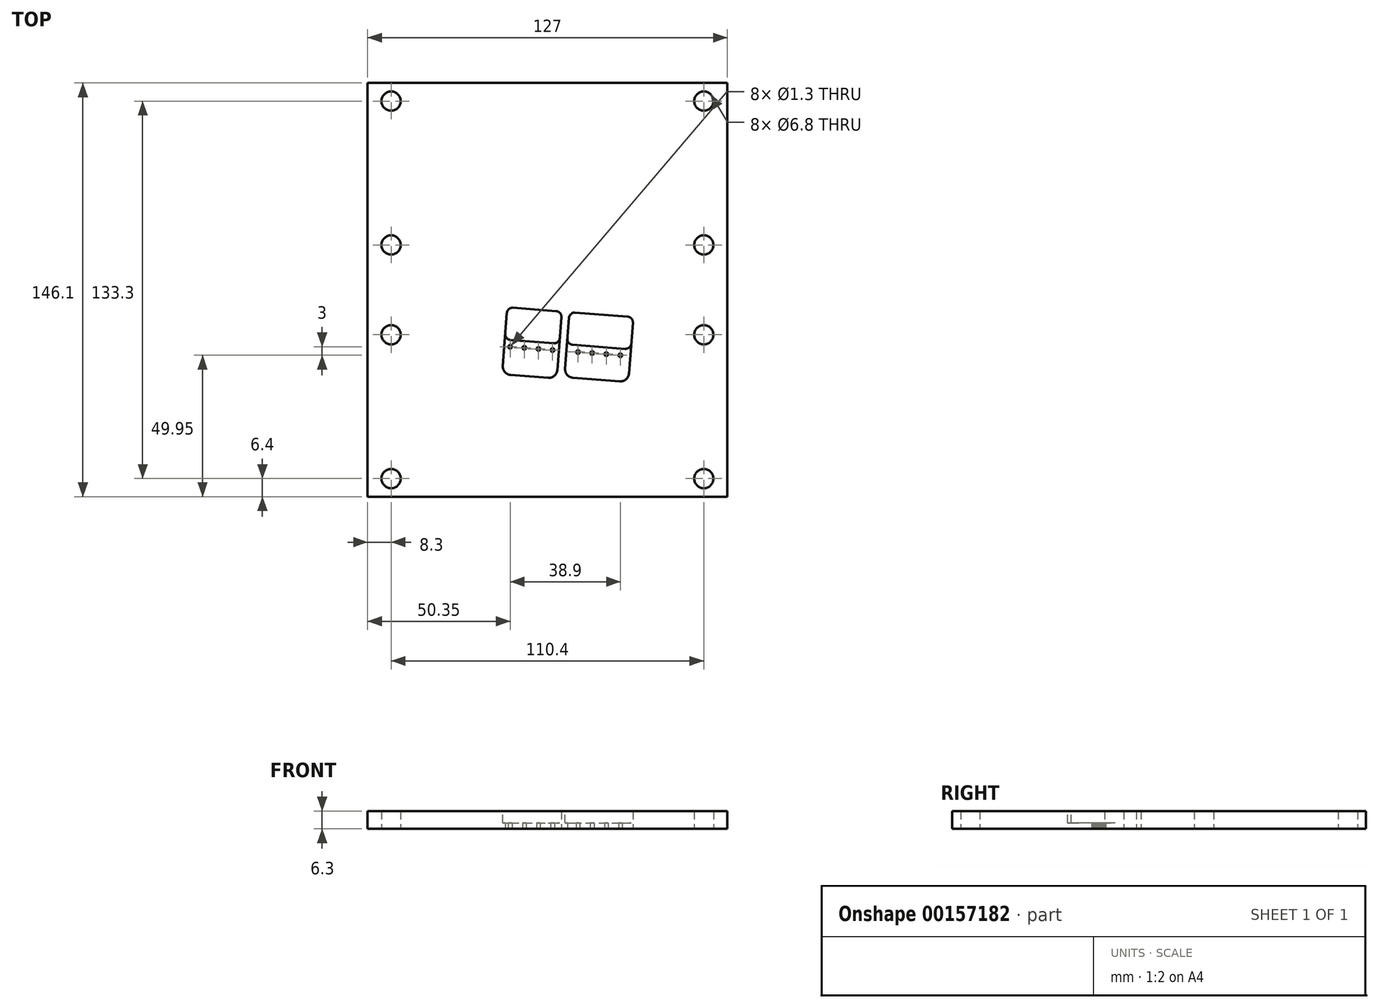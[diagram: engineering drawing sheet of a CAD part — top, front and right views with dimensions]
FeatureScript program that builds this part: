
annotation { "Feature Type Name" : "Feature", "Feature Type Description" : "" }
export const myFeature = defineFeature(function(context is Context, id is Id, definition is map)
    precondition{}
    {
        {
            var Q0;
            Q0=qCreatedBy(makeId("Top.planeOp"),FACE);
            var sketch = newSketch(context, id + "F0", { "sketchPlane" : qUnion([Q0])});
            skLineSegment(sketch, "E0.bottom", {"start": v(-63.5, 73.05) * mm, "end": v(63.5, 73.05) * mm});
            skLineSegment(sketch, "E0.top", {"start": v(-63.5, -73.05) * mm, "end": v(63.5, -73.05) * mm});
            skLineSegment(sketch, "E0.left", {"start": v(-63.5, 73.05) * mm, "end": v(-63.5, -73.05) * mm});
            skLineSegment(sketch, "E0.right", {"start": v(63.5, 73.05) * mm, "end": v(63.5, -73.05) * mm});
            skPoint(sketch, "E0.middle", {"position": v(0, 0) * mm});
            skLineSegment(sketch, "E1", {"start": v(-55.2, 73.05) * mm, "end": v(-55.2, -73.05) * mm, "construction": true});
            skLineSegment(sketch, "E2", {"start": v(55.2, 73.05) * mm, "end": v(55.2, -73.05) * mm, "construction": true});
            skCircle(sketch, "E3", {"center": v(-55.2, 66.65) * mm, "radius": 3.4 * mm});
            skCircle(sketch, "E4", {"center": v(-55.2, 15.85) * mm, "radius": 3.4 * mm});
            skCircle(sketch, "E5", {"center": v(-55.2, -15.85) * mm, "radius": 3.4 * mm});
            skCircle(sketch, "E6", {"center": v(-55.2, -66.65) * mm, "radius": 3.4 * mm});
            skCircle(sketch, "E7", {"center": v(55.2, -66.65) * mm, "radius": 3.4 * mm});
            skCircle(sketch, "E8", {"center": v(55.2, -15.85) * mm, "radius": 3.4 * mm});
            skCircle(sketch, "E9", {"center": v(55.2, 15.85) * mm, "radius": 3.4 * mm});
            skCircle(sketch, "E10", {"center": v(55.2, 66.65) * mm, "radius": 3.4 * mm});
            skCircle(sketch, "E11", {"center": v(25.75, -23.1) * mm, "radius": 0.65 * mm});
            skCircle(sketch, "E12", {"center": v(20.76, -22.72) * mm, "radius": 0.65 * mm});
            skCircle(sketch, "E13", {"center": v(15.78, -22.33) * mm, "radius": 0.65 * mm});
            skCircle(sketch, "E14", {"center": v(10.8, -21.95) * mm, "radius": 0.65 * mm});
            skCircle(sketch, "E15", {"center": v(1.8, -21.25) * mm, "radius": 0.65 * mm});
            skCircle(sketch, "E16", {"center": v(-3.18, -20.87) * mm, "radius": 0.65 * mm});
            skCircle(sketch, "E17", {"center": v(-8.16, -20.48) * mm, "radius": 0.65 * mm});
            skCircle(sketch, "E18", {"center": v(-13.15, -20.1) * mm, "radius": 0.65 * mm});
            skLineSegment(sketch, "E19", {"start": v(-13.15, -20.1) * mm, "end": v(25.75, -23.1) * mm, "construction": true});
            skLineSegment(sketch, "E20", {"start": v(-13.05, -17.7) * mm, "end": v(2.2, -18.88) * mm});
            skLineSegment(sketch, "E21", {"start": v(-12.17, -6.33) * mm, "end": v(3.08, -7.51) * mm});
            skLineSegment(sketch, "E22", {"start": v(-14.32, -8.17) * mm, "end": v(-14.89, -15.55) * mm});
            skLineSegment(sketch, "E23", {"start": v(4.92, -9.66) * mm, "end": v(4.35, -17.04) * mm});
            skLineSegment(sketch, "E24", {"start": v(7.61, -9.87) * mm, "end": v(7.04, -17.24) * mm});
            skLineSegment(sketch, "E25", {"start": v(30.15, -11.6) * mm, "end": v(29.58, -18.98) * mm});
            skLineSegment(sketch, "E26.trimOffspring", {"start": v(9.76, -8.03) * mm, "end": v(28.3, -9.46) * mm});
            skLineSegment(sketch, "E27.trimOffspring", {"start": v(8.89, -19.4) * mm, "end": v(27.43, -20.82) * mm});
            skPoint(sketch, "E28.visualSharp", {"position": v(-14.17, -6.18) * mm});
            skArc(sketch, "E28.filletArc", {"start": v(-12.17, -6.33) * mm, "mid": v(-13.63, -6.8) * mm, "end": v(-14.32, -8.17) * mm});
            skPoint(sketch, "E29.visualSharp", {"position": v(5.08, -7.66) * mm});
            skArc(sketch, "E29.filletArc", {"start": v(4.92, -9.66) * mm, "mid": v(4.45, -8.2) * mm, "end": v(3.08, -7.51) * mm});
            skPoint(sketch, "E30.visualSharp", {"position": v(-15.04, -17.55) * mm});
            skArc(sketch, "E30.filletArc", {"start": v(-14.89, -15.55) * mm, "mid": v(-14.41, -17) * mm, "end": v(-13.05, -17.7) * mm});
            skPoint(sketch, "E31.visualSharp", {"position": v(4.2, -19.03) * mm});
            skArc(sketch, "E31.filletArc", {"start": v(2.2, -18.88) * mm, "mid": v(3.66, -18.4) * mm, "end": v(4.35, -17.04) * mm});
            skPoint(sketch, "E32.visualSharp", {"position": v(7.77, -7.87) * mm});
            skArc(sketch, "E32.filletArc", {"start": v(9.76, -8.03) * mm, "mid": v(8.3, -8.5) * mm, "end": v(7.61, -9.87) * mm});
            skPoint(sketch, "E33.visualSharp", {"position": v(6.9, -19.24) * mm});
            skArc(sketch, "E33.filletArc", {"start": v(7.04, -17.24) * mm, "mid": v(7.52, -18.7) * mm, "end": v(8.89, -19.4) * mm});
            skPoint(sketch, "E34.visualSharp", {"position": v(30.3, -9.6) * mm});
            skArc(sketch, "E34.filletArc", {"start": v(30.15, -11.6) * mm, "mid": v(29.67, -10.15) * mm, "end": v(28.3, -9.46) * mm});
            skPoint(sketch, "E35.visualSharp", {"position": v(29.42, -20.98) * mm});
            skArc(sketch, "E35.filletArc", {"start": v(27.43, -20.82) * mm, "mid": v(28.89, -20.35) * mm, "end": v(29.58, -18.98) * mm});
            skSolve(sketch);
        }
        {
            var Q0;
            Q0 = qSketchRegion(id + "F0", true);
            extrude(context, id + "F1", {"entities" : qUnion([Q0]), "depth" : 6.3 * mm});
        }
        {
            var Q0;
            Q0=makeQuery(id+"F1.opExtrude","CAP_FACE",FACE,{"disambiguationData":[OSD([sQuery(id+"F0.wireOp",EDGE,"E0.bottom"),sQuery(id+"F0.wireOp",EDGE,"E0.top"),sQuery(id+"F0.wireOp",EDGE,"E0.left"),sQuery(id+"F0.wireOp",EDGE,"E0.right"),sQuery(id+"F0.wireOp",EDGE,"E3"),sQuery(id+"F0.wireOp",EDGE,"E4"),sQuery(id+"F0.wireOp",EDGE,"E5"),sQuery(id+"F0.wireOp",EDGE,"E6"),sQuery(id+"F0.wireOp",EDGE,"E7"),sQuery(id+"F0.wireOp",EDGE,"E8"),sQuery(id+"F0.wireOp",EDGE,"E9"),sQuery(id+"F0.wireOp",EDGE,"E10"),sQuery(id+"F0.wireOp",EDGE,"E11"),sQuery(id+"F0.wireOp",EDGE,"E12"),sQuery(id+"F0.wireOp",EDGE,"E13"),sQuery(id+"F0.wireOp",EDGE,"E14"),sQuery(id+"F0.wireOp",EDGE,"E15"),sQuery(id+"F0.wireOp",EDGE,"E16"),sQuery(id+"F0.wireOp",EDGE,"E17"),sQuery(id+"F0.wireOp",EDGE,"E18"),sQuery(id+"F0.wireOp",EDGE,"E20"),sQuery(id+"F0.wireOp",EDGE,"E21"),sQuery(id+"F0.wireOp",EDGE,"E22"),sQuery(id+"F0.wireOp",EDGE,"E23"),sQuery(id+"F0.wireOp",EDGE,"E24"),sQuery(id+"F0.wireOp",EDGE,"E25"),sQuery(id+"F0.wireOp",EDGE,"E26.trimOffspring"),sQuery(id+"F0.wireOp",EDGE,"E27.trimOffspring"),sQuery(id+"F0.wireOp",EDGE,"E28.filletArc"),sQuery(id+"F0.wireOp",EDGE,"E29.filletArc"),sQuery(id+"F0.wireOp",EDGE,"E30.filletArc"),sQuery(id+"F0.wireOp",EDGE,"E31.filletArc"),sQuery(id+"F0.wireOp",EDGE,"E32.filletArc"),sQuery(id+"F0.wireOp",EDGE,"E33.filletArc"),sQuery(id+"F0.wireOp",EDGE,"E34.filletArc"),sQuery(id+"F0.wireOp",EDGE,"E35.filletArc")])],"isStart":false});
            var sketch = newSketch(context, id + "F2", { "sketchPlane" : qUnion([Q0])});
            skLineSegment(sketch, "E36", {"start": v(-14.78, -14.1) * mm, "end": v(-15.76, -26.82) * mm});
            skLineSegment(sketch, "E37", {"start": v(-13, -30.04) * mm, "end": v(0.26, -31.06) * mm});
            skLineSegment(sketch, "E38", {"start": v(4.46, -15.58) * mm, "end": v(3.48, -28.3) * mm});
            skLineSegment(sketch, "E39", {"start": v(-14.78, -14.1) * mm, "end": v(4.46, -15.58) * mm});
            skLineSegment(sketch, "E40", {"start": v(7.17, -15.68) * mm, "end": v(6.23, -27.81) * mm});
            skLineSegment(sketch, "E41", {"start": v(9, -31.03) * mm, "end": v(25.54, -32.31) * mm});
            skLineSegment(sketch, "E42", {"start": v(29.7, -17.42) * mm, "end": v(28.76, -29.55) * mm});
            skLineSegment(sketch, "E43", {"start": v(7.17, -15.68) * mm, "end": v(29.7, -17.42) * mm});
            skPoint(sketch, "E44.visualSharp", {"position": v(6, -30.8) * mm});
            skArc(sketch, "E44.filletArc", {"start": v(6.23, -27.81) * mm, "mid": v(6.94, -30) * mm, "end": v(9, -31.03) * mm});
            skPoint(sketch, "E45.visualSharp", {"position": v(28.53, -32.54) * mm});
            skArc(sketch, "E45.filletArc", {"start": v(25.54, -32.31) * mm, "mid": v(27.72, -31.6) * mm, "end": v(28.76, -29.55) * mm});
            skPoint(sketch, "E46.visualSharp", {"position": v(3.25, -31.3) * mm});
            skArc(sketch, "E46.filletArc", {"start": v(0.26, -31.06) * mm, "mid": v(2.44, -30.35) * mm, "end": v(3.48, -28.3) * mm});
            skPoint(sketch, "E47.visualSharp", {"position": v(-15.99, -29.81) * mm});
            skArc(sketch, "E47.filletArc", {"start": v(-15.76, -26.82) * mm, "mid": v(-15.05, -29) * mm, "end": v(-13, -30.04) * mm});
            skSolve(sketch);
        }
        {
            var Q0;
            Q0 = qSketchRegion(id + "F2", true);
            extrude(context, id + "F3", {"entities" : qUnion([Q0]), "operationType" : NewBodyOperationType.REMOVE, "oppositeDirection" : true, "depth" : 4.25 * mm});
        }
    });
